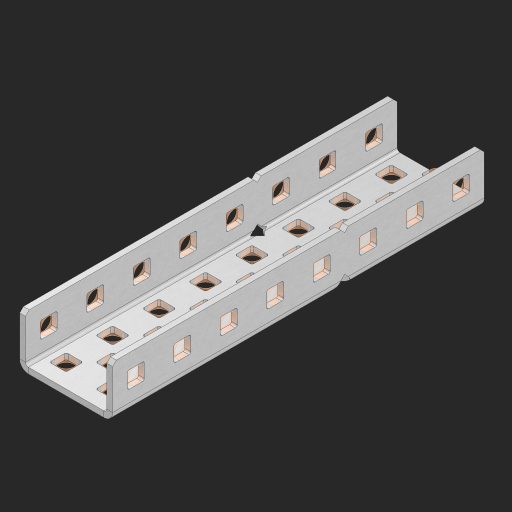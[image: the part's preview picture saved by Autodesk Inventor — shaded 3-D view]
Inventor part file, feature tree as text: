
AUTODESK INVENTOR PART (.ipt)
format: ipt  version: 2023 (Build 270158000, 158)  size: 849,920 bytes
history: native  units: in
note: dims shown in document units (in); Inventor stores cm internally (conversion verified against a paired STEP export)
features: other x47, extrude x38, sheet_metal_op x11, sketch x10, pattern_linear x2, mirror x1, chamfer x1
ambient origin geometry x8: Origin, YZ Plane, XZ Plane, XY Plane, X Axis, Y Axis, Z Axis, Center Point
bodies: Solid1 (feature_tree), Body (feature_tree)
feature tree (110):
  sheet_metal_op  "Flanges"
  other  "Flange Pattern Plane"
  other  "Flange Pattern Sketch"
  sheet_metal_op  "Flange Pattern"
  sheet_metal_op  "Body Pattern"
  pattern_linear  "Center Pattern"  Spacing1=0.0625in  [1 undecoded]
  other  "Arc Length"
  mirror  "Notch Mirror"
  pattern_linear  "Notch Pattern"  Spacing1=0.182in  [1 undecoded]
  chamfer  "End Chamfer"
  extrude  "Half Cut"  Depth=0.02in
  sketch  "Sketch1"  dims[d0=1.0in]
  other  "Plate1"
  sketch  "Sketch2"  dims[d1=4.0in]
  other  "Plate2"
  sheet_metal_op  "Bend1"
  sheet_metal_op  "Corner1"
  sketch  "Sketch3"  dims[d2=0.0625in]
  sketch  "Sketch7"  dims[d3=0.0625in]
  other  "Srf1"
  other  "Srf2"
  sketch  "Sketch8"  dims[d4=0.0312in]
  sketch  "Sketch9"  dims[d5=0.125in]
  other  "Srf91"
  sheet_metal_op  "Body Pattern Sketch"
  other  "Srf92"
  sketch  "Sketch13"  dims[d6=0.0625in]
  sketch  "Sketch14"  dims[d7=0.5in d8=90.0deg d9=0.0312in]
  sketch  "Sketch15"  dims[d10=0.25in]
  sketch  "Sketch16"  dims[d11=0.0625in d12=0.0625in d16=0.182in d17=0.02in d18=0.0625in d19=0.0in d20=0.25in d21=0.25in d38=3.1496in d40=0.5in d41=0.7874in d43=1.0in d46=0.172in d47=1.0in d48=0.0in d49=0.182in d50=0.02in d51=0.25in d52=0.25in d53=0.0625in d54=0.0in d55=0.172in d56=1.0in d57=0.0in d58=0.25in d60=3.1496in d62=0.5in d63=0.7874in d65=0.5in d85=0.1473in d86=0.1782in d88=0.04in d89=0.0625in d90=0.0in d91=0.04in d92=0.0491in d95=2.5in d96=0.04in d97=0.25in d98=45.0deg d99=0.25in d100=0.5in d101=0.0in d102=2.497in d106=0.182in d107=0.02in d108=0.5in d109=0.5in d110=0.0625in d111=0.0in d112=0.172in d113=0.5in d114=0.0in d117=0.5in d118=0.5in d119=0.5in]
  other  "Srf786"
  other  "Srf823"
  other  "Srf824"
  other  "Srf825"
  other  "Srf826"
  other  "Srf827"
  other  "Srf828"
  other  "Srf829"
  other  "Srf856"
  other  "Srf857"
  other  "Srf858"
  other  "Srf859"
  other  "Srf860"
  other  "Srf861"
  other  "Srf862"
  other  "Srf889"
  other  "Srf890"
  other  "Srf891"
  other  "Srf892"
  other  "Srf893"
  other  "Srf894"
  other  "Srf895"
  other  "Srf922"
  other  "Srf923"
  other  "Srf924"
  other  "Srf925"
  other  "Srf926"
  other  "Srf959"
  other  "Srf960"
  other  "Srf961"
  other  "Srf962"
  other  "Srf963"
  other  "Srf1143"
  other  "Srf1144"
  other  "Srf1199"
  other  "Srf1200"
  sheet_metal_op  "Flange Stamp"
  sheet_metal_op  "Flange Circle"
  sheet_metal_op  "Body Stamp"
  sheet_metal_op  "Body Circle"
  other  "Center Stamp"
  other  "Center Circle"
  sheet_metal_op  "Notch"
  extrude  "ExtrusionSrf2"  Depth=0.0625in
  extrude  "ExtrusionSrf92"  TaperAngle=0.0deg  [1 undecoded]
  extrude  "ExtrusionSrf823"  Depth=0.5in
  extrude  "ExtrusionSrf824"  Depth=0.5in
  extrude  "ExtrusionSrf825"  Depth=0.5in
  extrude  "ExtrusionSrf826"  Depth=0.5in
  extrude  "ExtrusionSrf827"  Depth=1.0in TaperAngle=0.0deg
  extrude  "ExtrusionSrf828"  Depth=0.5in
  extrude  "ExtrusionSrf829"  Depth=0.02in
  extrude  "ExtrusionSrf856"  Depth=0.5in
  extrude  "ExtrusionSrf857"  Depth=0.5in
  extrude  "ExtrusionSrf858"  Depth=0.0625in
  extrude  "ExtrusionSrf859"  TaperAngle=0.0deg  [1 undecoded]
  extrude  "ExtrusionSrf860"  Depth=0.5in
  extrude  "ExtrusionSrf861"  Depth=1.0in TaperAngle=0.0deg
  extrude  "ExtrusionSrf862"  Depth=0.5in
  extrude  "ExtrusionSrf889"  Depth=0.5in
  extrude  "ExtrusionSrf890"  Depth=0.5in
  extrude  "ExtrusionSrf891"  Depth=0.5in
  extrude  "ExtrusionSrf892"  Depth=0.5in
  extrude  "ExtrusionSrf893"  Depth=0.5in
  extrude  "ExtrusionSrf894"  Depth=0.0625in
  extrude  "ExtrusionSrf895"  TaperAngle=0.0deg  [1 undecoded]
  extrude  "ExtrusionSrf922"  Depth=0.5in
  extrude  "ExtrusionSrf923"  Depth=0.5in
  extrude  "ExtrusionSrf924"  Depth=2.5in
  extrude  "ExtrusionSrf925"  Depth=0.5in TaperAngle=45.0deg
  extrude  "ExtrusionSrf926"  Depth=0.5in
  extrude  "ExtrusionSrf959"  Depth=0.5in TaperAngle=0.0deg
  extrude  "ExtrusionSrf960"  Depth=0.5in
  extrude  "ExtrusionSrf961"  Depth=0.5in
  extrude  "ExtrusionSrf962"  Depth=0.02in
  extrude  "ExtrusionSrf963"  Depth=0.5in
  extrude  "ExtrusionSrf1143"  Depth=0.5in
  extrude  "ExtrusionSrf1144"  Depth=0.0625in
  extrude  "ExtrusionSrf1199"  TaperAngle=0.0deg  [1 undecoded]
  extrude  "ExtrusionSrf1200"  Depth=0.5in
note: 6 required parameter values undecoded (feature->parameter linkage not recoverable at this tier; creation-order binding heuristic only, values carry confidence <= 0.55)
